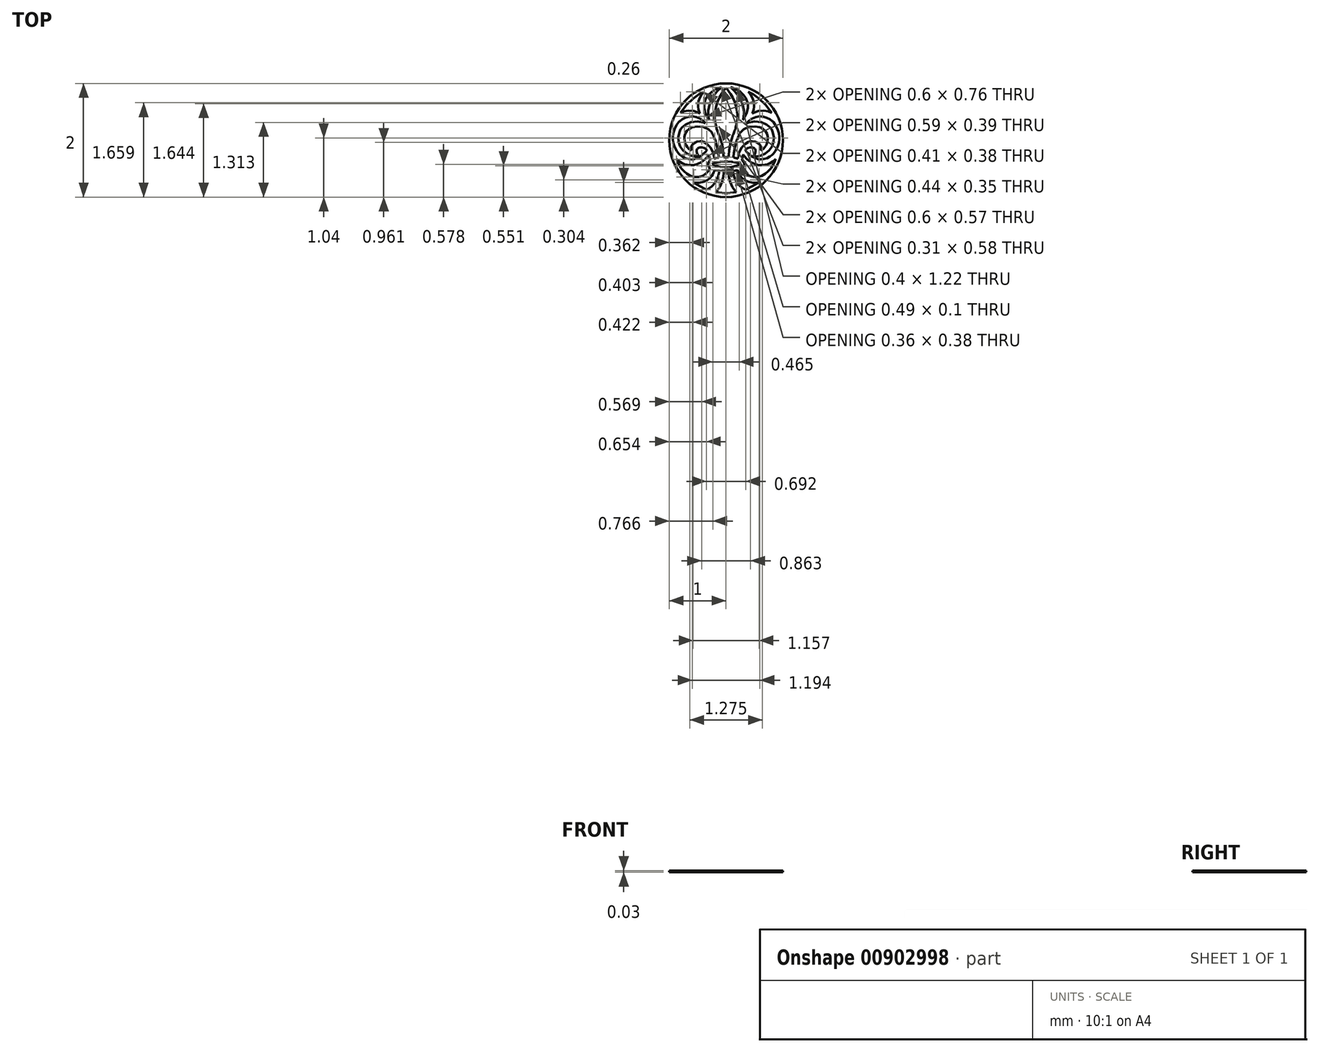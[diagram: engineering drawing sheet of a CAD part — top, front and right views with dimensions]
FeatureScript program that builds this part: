
annotation { "Feature Type Name" : "Feature", "Feature Type Description" : "" }
export const myFeature = defineFeature(function(context is Context, id is Id, definition is map)
    precondition{}
    {
        {
            var Q0;
            Q0=qCreatedBy(makeId("Top.planeOp"),FACE);
            var sketch = newSketch(context, id + "F0", { "sketchPlane" : qUnion([Q0])});
            skLineSegment(sketch, "E0", {"start": v(-0.6, -0.34) * mm, "end": v(-0.58, -0.34) * mm});
            skLineSegment(sketch, "E1", {"start": v(-0.58, -0.34) * mm, "end": v(-0.46, -0.3) * mm});
            skLineSegment(sketch, "E2", {"start": v(-0.46, -0.3) * mm, "end": v(-0.36, -0.2) * mm});
            skLineSegment(sketch, "E3", {"start": v(-0.36, -0.2) * mm, "end": v(-0.34, -0.18) * mm});
            skLineSegment(sketch, "E4", {"start": v(-0.34, -0.18) * mm, "end": v(-0.34, -0.17) * mm});
            skLineSegment(sketch, "E5", {"start": v(-0.34, -0.17) * mm, "end": v(-0.35, -0.16) * mm});
            skLineSegment(sketch, "E6", {"start": v(-0.35, -0.16) * mm, "end": v(-0.37, -0.15) * mm});
            skLineSegment(sketch, "E7", {"start": v(-0.37, -0.15) * mm, "end": v(-0.37, -0.15) * mm});
            skLineSegment(sketch, "E8", {"start": v(-0.37, -0.15) * mm, "end": v(-0.38, -0.14) * mm});
            skLineSegment(sketch, "E9", {"start": v(-0.38, -0.14) * mm, "end": v(-0.42, -0.13) * mm});
            skLineSegment(sketch, "E10", {"start": v(-0.42, -0.13) * mm, "end": v(-0.47, -0.13) * mm});
            skLineSegment(sketch, "E11", {"start": v(-0.47, -0.13) * mm, "end": v(-0.48, -0.13) * mm});
            skLineSegment(sketch, "E12", {"start": v(-0.48, -0.13) * mm, "end": v(-0.48, -0.13) * mm});
            skLineSegment(sketch, "E13", {"start": v(-0.48, -0.13) * mm, "end": v(-0.5, -0.15) * mm});
            skLineSegment(sketch, "E14", {"start": v(-0.5, -0.15) * mm, "end": v(-0.52, -0.17) * mm});
            skLineSegment(sketch, "E15", {"start": v(-0.52, -0.17) * mm, "end": v(-0.52, -0.18) * mm});
            skLineSegment(sketch, "E16", {"start": v(-0.52, -0.18) * mm, "end": v(-0.52, -0.18) * mm});
            skLineSegment(sketch, "E17", {"start": v(-0.52, -0.18) * mm, "end": v(-0.52, -0.2) * mm});
            skLineSegment(sketch, "E18", {"start": v(-0.52, -0.2) * mm, "end": v(-0.51, -0.23) * mm});
            skLineSegment(sketch, "E19", {"start": v(-0.51, -0.23) * mm, "end": v(-0.5, -0.25) * mm});
            skLineSegment(sketch, "E20", {"start": v(-0.5, -0.25) * mm, "end": v(-0.5, -0.26) * mm});
            skLineSegment(sketch, "E21", {"start": v(-0.5, -0.26) * mm, "end": v(-0.5, -0.26) * mm});
            skLineSegment(sketch, "E22", {"start": v(-0.5, -0.26) * mm, "end": v(-0.47, -0.29) * mm});
            skLineSegment(sketch, "E23", {"start": v(-0.47, -0.29) * mm, "end": v(-0.5, -0.29) * mm});
            skLineSegment(sketch, "E24", {"start": v(-0.5, -0.29) * mm, "end": v(-0.53, -0.29) * mm});
            skLineSegment(sketch, "E25", {"start": v(-0.53, -0.29) * mm, "end": v(-0.6, -0.27) * mm});
            skLineSegment(sketch, "E26", {"start": v(-0.6, -0.27) * mm, "end": v(-0.69, -0.23) * mm});
            skLineSegment(sketch, "E27", {"start": v(-0.69, -0.23) * mm, "end": v(-0.76, -0.18) * mm});
            skLineSegment(sketch, "E28", {"start": v(-0.76, -0.18) * mm, "end": v(-0.8, -0.13) * mm});
            skLineSegment(sketch, "E29", {"start": v(-0.8, -0.13) * mm, "end": v(-0.8, -0.1) * mm});
            skLineSegment(sketch, "E30", {"start": v(-0.8, -0.1) * mm, "end": v(-0.82, -0.09) * mm});
            skLineSegment(sketch, "E31", {"start": v(-0.82, -0.09) * mm, "end": v(-0.84, -0.03) * mm});
            skLineSegment(sketch, "E32", {"start": v(-0.84, -0.03) * mm, "end": v(-0.84, 0.05) * mm});
            skLineSegment(sketch, "E33", {"start": v(-0.84, 0.05) * mm, "end": v(-0.83, 0.13) * mm});
            skLineSegment(sketch, "E34", {"start": v(-0.83, 0.13) * mm, "end": v(-0.8, 0.19) * mm});
            skLineSegment(sketch, "E35", {"start": v(-0.8, 0.19) * mm, "end": v(-0.79, 0.2) * mm});
            skLineSegment(sketch, "E36", {"start": v(-0.79, 0.2) * mm, "end": v(-0.77, 0.22) * mm});
            skLineSegment(sketch, "E37", {"start": v(-0.77, 0.22) * mm, "end": v(-0.72, 0.28) * mm});
            skLineSegment(sketch, "E38", {"start": v(-0.72, 0.28) * mm, "end": v(-0.62, 0.32) * mm});
            skLineSegment(sketch, "E39", {"start": v(-0.62, 0.32) * mm, "end": v(-0.5, 0.33) * mm});
            skLineSegment(sketch, "E40", {"start": v(-0.5, 0.33) * mm, "end": v(-0.4, 0.31) * mm});
            skLineSegment(sketch, "E41", {"start": v(-0.4, 0.31) * mm, "end": v(-0.36, 0.3) * mm});
            skLineSegment(sketch, "E42", {"start": v(-0.36, 0.3) * mm, "end": v(-0.37, 0.31) * mm});
            skLineSegment(sketch, "E43", {"start": v(-0.37, 0.31) * mm, "end": v(-0.4, 0.34) * mm});
            skLineSegment(sketch, "E44", {"start": v(-0.4, 0.34) * mm, "end": v(-0.46, 0.38) * mm});
            skLineSegment(sketch, "E45", {"start": v(-0.46, 0.38) * mm, "end": v(-0.52, 0.4) * mm});
            skLineSegment(sketch, "E46", {"start": v(-0.52, 0.4) * mm, "end": v(-0.58, 0.42) * mm});
            skLineSegment(sketch, "E47", {"start": v(-0.58, 0.42) * mm, "end": v(-0.6, 0.42) * mm});
            skLineSegment(sketch, "E48", {"start": v(-0.6, 0.42) * mm, "end": v(-0.62, 0.42) * mm});
            skLineSegment(sketch, "E49", {"start": v(-0.62, 0.42) * mm, "end": v(-0.66, 0.41) * mm});
            skLineSegment(sketch, "E50", {"start": v(-0.66, 0.41) * mm, "end": v(-0.72, 0.4) * mm});
            skLineSegment(sketch, "E51", {"start": v(-0.72, 0.4) * mm, "end": v(-0.77, 0.37) * mm});
            skLineSegment(sketch, "E52", {"start": v(-0.77, 0.37) * mm, "end": v(-0.8, 0.34) * mm});
            skLineSegment(sketch, "E53", {"start": v(-0.8, 0.34) * mm, "end": v(-0.82, 0.33) * mm});
            skLineSegment(sketch, "E54", {"start": v(-0.82, 0.33) * mm, "end": v(-0.83, 0.31) * mm});
            skLineSegment(sketch, "E55", {"start": v(-0.83, 0.31) * mm, "end": v(-0.87, 0.27) * mm});
            skLineSegment(sketch, "E56", {"start": v(-0.87, 0.27) * mm, "end": v(-0.9, 0.2) * mm});
            skLineSegment(sketch, "E57", {"start": v(-0.9, 0.2) * mm, "end": v(-0.93, 0.12) * mm});
            skLineSegment(sketch, "E58", {"start": v(-0.93, 0.12) * mm, "end": v(-0.94, 0.06) * mm});
            skLineSegment(sketch, "E59", {"start": v(-0.94, 0.06) * mm, "end": v(-0.94, 0.04) * mm});
            skLineSegment(sketch, "E60", {"start": v(-0.94, 0.04) * mm, "end": v(-0.94, 0.02) * mm});
            skLineSegment(sketch, "E61", {"start": v(-0.94, 0.02) * mm, "end": v(-0.93, -0.04) * mm});
            skLineSegment(sketch, "E62", {"start": v(-0.93, -0.04) * mm, "end": v(-0.9, -0.12) * mm});
            skLineSegment(sketch, "E63", {"start": v(-0.9, -0.12) * mm, "end": v(-0.87, -0.19) * mm});
            skLineSegment(sketch, "E64", {"start": v(-0.87, -0.19) * mm, "end": v(-0.83, -0.24) * mm});
            skLineSegment(sketch, "E65", {"start": v(-0.83, -0.24) * mm, "end": v(-0.82, -0.25) * mm});
            skLineSegment(sketch, "E66", {"start": v(-0.82, -0.25) * mm, "end": v(-0.8, -0.26) * mm});
            skLineSegment(sketch, "E67", {"start": v(-0.8, -0.26) * mm, "end": v(-0.77, -0.29) * mm});
            skLineSegment(sketch, "E68", {"start": v(-0.77, -0.29) * mm, "end": v(-0.72, -0.32) * mm});
            skLineSegment(sketch, "E69", {"start": v(-0.72, -0.32) * mm, "end": v(-0.66, -0.33) * mm});
            skLineSegment(sketch, "E70", {"start": v(-0.66, -0.33) * mm, "end": v(-0.62, -0.34) * mm});
            skLineSegment(sketch, "E71", {"start": v(-0.62, -0.34) * mm, "end": v(-0.6, -0.34) * mm});
            skLineSegment(sketch, "E72", {"start": v(-0.29, -0.48) * mm, "end": v(-0.3, -0.48) * mm});
            skLineSegment(sketch, "E73", {"start": v(-0.3, -0.48) * mm, "end": v(-0.31, -0.45) * mm});
            skLineSegment(sketch, "E74", {"start": v(-0.31, -0.45) * mm, "end": v(-0.32, -0.43) * mm});
            skLineSegment(sketch, "E75", {"start": v(-0.32, -0.43) * mm, "end": v(-0.32, -0.42) * mm});
            skLineSegment(sketch, "E76", {"start": v(-0.32, -0.42) * mm, "end": v(-0.32, -0.41) * mm});
            skLineSegment(sketch, "E77", {"start": v(-0.32, -0.41) * mm, "end": v(-0.31, -0.4) * mm});
            skLineSegment(sketch, "E78", {"start": v(-0.31, -0.4) * mm, "end": v(-0.3, -0.36) * mm});
            skLineSegment(sketch, "E79", {"start": v(-0.3, -0.36) * mm, "end": v(-0.28, -0.36) * mm});
            skLineSegment(sketch, "E80", {"start": v(-0.28, -0.36) * mm, "end": v(-0.28, -0.35) * mm});
            skLineSegment(sketch, "E81", {"start": v(-0.28, -0.35) * mm, "end": v(-0.29, -0.3) * mm});
            skLineSegment(sketch, "E82", {"start": v(-0.29, -0.3) * mm, "end": v(-0.3, -0.26) * mm});
            skLineSegment(sketch, "E83", {"start": v(-0.3, -0.26) * mm, "end": v(-0.3, -0.25) * mm});
            skLineSegment(sketch, "E84", {"start": v(-0.3, -0.25) * mm, "end": v(-0.31, -0.27) * mm});
            skLineSegment(sketch, "E85", {"start": v(-0.31, -0.27) * mm, "end": v(-0.37, -0.33) * mm});
            skLineSegment(sketch, "E86", {"start": v(-0.37, -0.33) * mm, "end": v(-0.44, -0.39) * mm});
            skLineSegment(sketch, "E87", {"start": v(-0.44, -0.39) * mm, "end": v(-0.5, -0.42) * mm});
            skLineSegment(sketch, "E88", {"start": v(-0.5, -0.42) * mm, "end": v(-0.57, -0.44) * mm});
            skLineSegment(sketch, "E89", {"start": v(-0.57, -0.44) * mm, "end": v(-0.63, -0.44) * mm});
            skLineSegment(sketch, "E90", {"start": v(-0.63, -0.44) * mm, "end": v(-0.68, -0.43) * mm});
            skLineSegment(sketch, "E91", {"start": v(-0.68, -0.43) * mm, "end": v(-0.73, -0.42) * mm});
            skLineSegment(sketch, "E92", {"start": v(-0.73, -0.42) * mm, "end": v(-0.75, -0.42) * mm});
            skLineSegment(sketch, "E93", {"start": v(-0.75, -0.42) * mm, "end": v(-0.76, -0.41) * mm});
            skLineSegment(sketch, "E94", {"start": v(-0.76, -0.41) * mm, "end": v(-0.77, -0.4) * mm});
            skLineSegment(sketch, "E95", {"start": v(-0.77, -0.4) * mm, "end": v(-0.83, -0.37) * mm});
            skLineSegment(sketch, "E96", {"start": v(-0.83, -0.37) * mm, "end": v(-0.87, -0.34) * mm});
            skLineSegment(sketch, "E97", {"start": v(-0.87, -0.34) * mm, "end": v(-0.87, -0.33) * mm});
            skLineSegment(sketch, "E98", {"start": v(-0.87, -0.33) * mm, "end": v(-0.87, -0.34) * mm});
            skLineSegment(sketch, "E99", {"start": v(-0.87, -0.34) * mm, "end": v(-0.85, -0.38) * mm});
            skLineSegment(sketch, "E100", {"start": v(-0.85, -0.38) * mm, "end": v(-0.82, -0.44) * mm});
            skLineSegment(sketch, "E101", {"start": v(-0.82, -0.44) * mm, "end": v(-0.79, -0.5) * mm});
            skLineSegment(sketch, "E102", {"start": v(-0.79, -0.5) * mm, "end": v(-0.74, -0.55) * mm});
            skLineSegment(sketch, "E103", {"start": v(-0.74, -0.55) * mm, "end": v(-0.69, -0.6) * mm});
            skLineSegment(sketch, "E104", {"start": v(-0.69, -0.6) * mm, "end": v(-0.62, -0.63) * mm});
            skLineSegment(sketch, "E105", {"start": v(-0.62, -0.63) * mm, "end": v(-0.55, -0.64) * mm});
            skLineSegment(sketch, "E106", {"start": v(-0.55, -0.64) * mm, "end": v(-0.48, -0.65) * mm});
            skLineSegment(sketch, "E107", {"start": v(-0.48, -0.65) * mm, "end": v(-0.46, -0.64) * mm});
            skLineSegment(sketch, "E108", {"start": v(-0.46, -0.64) * mm, "end": v(-0.44, -0.64) * mm});
            skLineSegment(sketch, "E109", {"start": v(-0.44, -0.64) * mm, "end": v(-0.4, -0.62) * mm});
            skLineSegment(sketch, "E110", {"start": v(-0.4, -0.62) * mm, "end": v(-0.35, -0.59) * mm});
            skLineSegment(sketch, "E111", {"start": v(-0.35, -0.59) * mm, "end": v(-0.31, -0.54) * mm});
            skLineSegment(sketch, "E112", {"start": v(-0.31, -0.54) * mm, "end": v(-0.3, -0.5) * mm});
            skLineSegment(sketch, "E113", {"start": v(-0.3, -0.5) * mm, "end": v(-0.29, -0.48) * mm});
            skLineSegment(sketch, "E114", {"start": v(0.6, -0.34) * mm, "end": v(0.62, -0.34) * mm});
            skLineSegment(sketch, "E115", {"start": v(0.62, -0.34) * mm, "end": v(0.66, -0.33) * mm});
            skLineSegment(sketch, "E116", {"start": v(0.66, -0.33) * mm, "end": v(0.72, -0.32) * mm});
            skLineSegment(sketch, "E117", {"start": v(0.72, -0.32) * mm, "end": v(0.77, -0.29) * mm});
            skLineSegment(sketch, "E118", {"start": v(0.77, -0.29) * mm, "end": v(0.8, -0.26) * mm});
            skLineSegment(sketch, "E119", {"start": v(0.8, -0.26) * mm, "end": v(0.82, -0.25) * mm});
            skLineSegment(sketch, "E120", {"start": v(0.82, -0.25) * mm, "end": v(0.83, -0.24) * mm});
            skLineSegment(sketch, "E121", {"start": v(0.83, -0.24) * mm, "end": v(0.87, -0.19) * mm});
            skLineSegment(sketch, "E122", {"start": v(0.87, -0.19) * mm, "end": v(0.9, -0.12) * mm});
            skLineSegment(sketch, "E123", {"start": v(0.9, -0.12) * mm, "end": v(0.93, -0.04) * mm});
            skLineSegment(sketch, "E124", {"start": v(0.93, -0.04) * mm, "end": v(0.94, 0.02) * mm});
            skLineSegment(sketch, "E125", {"start": v(0.94, 0.02) * mm, "end": v(0.94, 0.04) * mm});
            skLineSegment(sketch, "E126", {"start": v(0.94, 0.04) * mm, "end": v(0.94, 0.06) * mm});
            skLineSegment(sketch, "E127", {"start": v(0.94, 0.06) * mm, "end": v(0.93, 0.12) * mm});
            skLineSegment(sketch, "E128", {"start": v(0.93, 0.12) * mm, "end": v(0.9, 0.2) * mm});
            skLineSegment(sketch, "E129", {"start": v(0.9, 0.2) * mm, "end": v(0.87, 0.27) * mm});
            skLineSegment(sketch, "E130", {"start": v(0.87, 0.27) * mm, "end": v(0.83, 0.31) * mm});
            skLineSegment(sketch, "E131", {"start": v(0.83, 0.31) * mm, "end": v(0.82, 0.33) * mm});
            skLineSegment(sketch, "E132", {"start": v(0.82, 0.33) * mm, "end": v(0.8, 0.34) * mm});
            skLineSegment(sketch, "E133", {"start": v(0.8, 0.34) * mm, "end": v(0.77, 0.37) * mm});
            skLineSegment(sketch, "E134", {"start": v(0.77, 0.37) * mm, "end": v(0.72, 0.4) * mm});
            skLineSegment(sketch, "E135", {"start": v(0.72, 0.4) * mm, "end": v(0.66, 0.41) * mm});
            skLineSegment(sketch, "E136", {"start": v(0.66, 0.41) * mm, "end": v(0.62, 0.42) * mm});
            skLineSegment(sketch, "E137", {"start": v(0.62, 0.42) * mm, "end": v(0.6, 0.42) * mm});
            skLineSegment(sketch, "E138", {"start": v(0.6, 0.42) * mm, "end": v(0.58, 0.42) * mm});
            skLineSegment(sketch, "E139", {"start": v(0.58, 0.42) * mm, "end": v(0.52, 0.4) * mm});
            skLineSegment(sketch, "E140", {"start": v(0.52, 0.4) * mm, "end": v(0.46, 0.38) * mm});
            skLineSegment(sketch, "E141", {"start": v(0.46, 0.38) * mm, "end": v(0.4, 0.34) * mm});
            skLineSegment(sketch, "E142", {"start": v(0.4, 0.34) * mm, "end": v(0.37, 0.31) * mm});
            skLineSegment(sketch, "E143", {"start": v(0.37, 0.31) * mm, "end": v(0.36, 0.3) * mm});
            skLineSegment(sketch, "E144", {"start": v(0.36, 0.3) * mm, "end": v(0.4, 0.31) * mm});
            skLineSegment(sketch, "E145", {"start": v(0.4, 0.31) * mm, "end": v(0.5, 0.33) * mm});
            skLineSegment(sketch, "E146", {"start": v(0.5, 0.33) * mm, "end": v(0.62, 0.32) * mm});
            skLineSegment(sketch, "E147", {"start": v(0.62, 0.32) * mm, "end": v(0.72, 0.28) * mm});
            skLineSegment(sketch, "E148", {"start": v(0.72, 0.28) * mm, "end": v(0.77, 0.22) * mm});
            skLineSegment(sketch, "E149", {"start": v(0.77, 0.22) * mm, "end": v(0.79, 0.2) * mm});
            skLineSegment(sketch, "E150", {"start": v(0.79, 0.2) * mm, "end": v(0.8, 0.19) * mm});
            skLineSegment(sketch, "E151", {"start": v(0.8, 0.19) * mm, "end": v(0.83, 0.13) * mm});
            skLineSegment(sketch, "E152", {"start": v(0.83, 0.13) * mm, "end": v(0.84, 0.05) * mm});
            skLineSegment(sketch, "E153", {"start": v(0.84, 0.05) * mm, "end": v(0.84, -0.03) * mm});
            skLineSegment(sketch, "E154", {"start": v(0.84, -0.03) * mm, "end": v(0.82, -0.09) * mm});
            skLineSegment(sketch, "E155", {"start": v(0.82, -0.09) * mm, "end": v(0.8, -0.1) * mm});
            skLineSegment(sketch, "E156", {"start": v(0.8, -0.1) * mm, "end": v(0.8, -0.13) * mm});
            skLineSegment(sketch, "E157", {"start": v(0.8, -0.13) * mm, "end": v(0.76, -0.18) * mm});
            skLineSegment(sketch, "E158", {"start": v(0.76, -0.18) * mm, "end": v(0.69, -0.23) * mm});
            skLineSegment(sketch, "E159", {"start": v(0.69, -0.23) * mm, "end": v(0.6, -0.27) * mm});
            skLineSegment(sketch, "E160", {"start": v(0.6, -0.27) * mm, "end": v(0.53, -0.29) * mm});
            skLineSegment(sketch, "E161", {"start": v(0.53, -0.29) * mm, "end": v(0.5, -0.29) * mm});
            skLineSegment(sketch, "E162", {"start": v(0.5, -0.29) * mm, "end": v(0.47, -0.29) * mm});
            skLineSegment(sketch, "E163", {"start": v(0.47, -0.29) * mm, "end": v(0.5, -0.26) * mm});
            skLineSegment(sketch, "E164", {"start": v(0.5, -0.26) * mm, "end": v(0.5, -0.26) * mm});
            skLineSegment(sketch, "E165", {"start": v(0.5, -0.26) * mm, "end": v(0.5, -0.25) * mm});
            skLineSegment(sketch, "E166", {"start": v(0.5, -0.25) * mm, "end": v(0.51, -0.23) * mm});
            skLineSegment(sketch, "E167", {"start": v(0.51, -0.23) * mm, "end": v(0.52, -0.2) * mm});
            skLineSegment(sketch, "E168", {"start": v(0.52, -0.2) * mm, "end": v(0.52, -0.18) * mm});
            skLineSegment(sketch, "E169", {"start": v(0.52, -0.18) * mm, "end": v(0.52, -0.18) * mm});
            skLineSegment(sketch, "E170", {"start": v(0.52, -0.18) * mm, "end": v(0.52, -0.17) * mm});
            skLineSegment(sketch, "E171", {"start": v(0.52, -0.17) * mm, "end": v(0.5, -0.15) * mm});
            skLineSegment(sketch, "E172", {"start": v(0.5, -0.15) * mm, "end": v(0.48, -0.13) * mm});
            skLineSegment(sketch, "E173", {"start": v(0.48, -0.13) * mm, "end": v(0.48, -0.13) * mm});
            skLineSegment(sketch, "E174", {"start": v(0.48, -0.13) * mm, "end": v(0.47, -0.13) * mm});
            skLineSegment(sketch, "E175", {"start": v(0.47, -0.13) * mm, "end": v(0.42, -0.13) * mm});
            skLineSegment(sketch, "E176", {"start": v(0.42, -0.13) * mm, "end": v(0.38, -0.14) * mm});
            skLineSegment(sketch, "E177", {"start": v(0.38, -0.14) * mm, "end": v(0.37, -0.15) * mm});
            skLineSegment(sketch, "E178", {"start": v(0.37, -0.15) * mm, "end": v(0.37, -0.15) * mm});
            skLineSegment(sketch, "E179", {"start": v(0.37, -0.15) * mm, "end": v(0.35, -0.16) * mm});
            skLineSegment(sketch, "E180", {"start": v(0.35, -0.16) * mm, "end": v(0.34, -0.17) * mm});
            skLineSegment(sketch, "E181", {"start": v(0.34, -0.17) * mm, "end": v(0.34, -0.18) * mm});
            skLineSegment(sketch, "E182", {"start": v(0.34, -0.18) * mm, "end": v(0.36, -0.2) * mm});
            skLineSegment(sketch, "E183", {"start": v(0.36, -0.2) * mm, "end": v(0.46, -0.3) * mm});
            skLineSegment(sketch, "E184", {"start": v(0.46, -0.3) * mm, "end": v(0.58, -0.34) * mm});
            skLineSegment(sketch, "E185", {"start": v(0.58, -0.34) * mm, "end": v(0.6, -0.34) * mm});
            skLineSegment(sketch, "E186", {"start": v(-0.17, 0.2) * mm, "end": v(-0.12, 0.1) * mm});
            skLineSegment(sketch, "E187", {"start": v(-0.12, 0.1) * mm, "end": v(-0.12, 0.08) * mm});
            skLineSegment(sketch, "E188", {"start": v(-0.12, 0.08) * mm, "end": v(-0.1, 0.02) * mm});
            skLineSegment(sketch, "E189", {"start": v(-0.1, 0.02) * mm, "end": v(-0.08, -0.04) * mm});
            skLineSegment(sketch, "E190", {"start": v(-0.08, -0.04) * mm, "end": v(-0.08, -0.06) * mm});
            skLineSegment(sketch, "E191", {"start": v(-0.08, -0.06) * mm, "end": v(-0.07, -0.08) * mm});
            skLineSegment(sketch, "E192", {"start": v(-0.07, -0.08) * mm, "end": v(-0.05, -0.18) * mm});
            skLineSegment(sketch, "E193", {"start": v(-0.05, -0.18) * mm, "end": v(-0.04, -0.27) * mm});
            skLineSegment(sketch, "E194", {"start": v(-0.04, -0.27) * mm, "end": v(-0.04, -0.28) * mm});
            skLineSegment(sketch, "E195", {"start": v(-0.04, -0.28) * mm, "end": v(-0.04, -0.3) * mm});
            skLineSegment(sketch, "E196", {"start": v(-0.04, -0.3) * mm, "end": v(-0.04, -0.3) * mm});
            skLineSegment(sketch, "E197", {"start": v(-0.04, -0.3) * mm, "end": v(-0.02, -0.3) * mm});
            skLineSegment(sketch, "E198", {"start": v(-0.02, -0.3) * mm, "end": v(0, -0.3) * mm});
            skLineSegment(sketch, "E199", {"start": v(0, -0.3) * mm, "end": v(0, -0.3) * mm});
            skLineSegment(sketch, "E200", {"start": v(0, -0.3) * mm, "end": v(0.02, -0.3) * mm});
            skLineSegment(sketch, "E201", {"start": v(0.02, -0.3) * mm, "end": v(0.04, -0.3) * mm});
            skLineSegment(sketch, "E202", {"start": v(0.04, -0.3) * mm, "end": v(0.04, -0.3) * mm});
            skLineSegment(sketch, "E203", {"start": v(0.04, -0.3) * mm, "end": v(0.04, -0.28) * mm});
            skLineSegment(sketch, "E204", {"start": v(0.04, -0.28) * mm, "end": v(0.04, -0.27) * mm});
            skLineSegment(sketch, "E205", {"start": v(0.04, -0.27) * mm, "end": v(0.05, -0.18) * mm});
            skLineSegment(sketch, "E206", {"start": v(0.05, -0.18) * mm, "end": v(0.07, -0.08) * mm});
            skLineSegment(sketch, "E207", {"start": v(0.07, -0.08) * mm, "end": v(0.08, -0.06) * mm});
            skLineSegment(sketch, "E208", {"start": v(0.08, -0.06) * mm, "end": v(0.08, -0.04) * mm});
            skLineSegment(sketch, "E209", {"start": v(0.08, -0.04) * mm, "end": v(0.1, 0.02) * mm});
            skLineSegment(sketch, "E210", {"start": v(0.1, 0.02) * mm, "end": v(0.12, 0.08) * mm});
            skLineSegment(sketch, "E211", {"start": v(0.12, 0.08) * mm, "end": v(0.12, 0.1) * mm});
            skLineSegment(sketch, "E212", {"start": v(0.12, 0.1) * mm, "end": v(0.13, 0.1) * mm});
            skLineSegment(sketch, "E213", {"start": v(0.13, 0.1) * mm, "end": v(0.13, 0.1) * mm});
            skLineSegment(sketch, "E214", {"start": v(0.13, 0.1) * mm, "end": v(0.14, 0.13) * mm});
            skLineSegment(sketch, "E215", {"start": v(0.14, 0.13) * mm, "end": v(0.14, 0.15) * mm});
            skLineSegment(sketch, "E216", {"start": v(0.14, 0.15) * mm, "end": v(0.15, 0.17) * mm});
            skLineSegment(sketch, "E217", {"start": v(0.15, 0.17) * mm, "end": v(0.16, 0.19) * mm});
            skLineSegment(sketch, "E218", {"start": v(0.16, 0.19) * mm, "end": v(0.16, 0.2) * mm});
            skLineSegment(sketch, "E219", {"start": v(0.16, 0.2) * mm, "end": v(0.17, 0.2) * mm});
            skLineSegment(sketch, "E220", {"start": v(0.17, 0.2) * mm, "end": v(0.17, 0.2) * mm});
            skLineSegment(sketch, "E221", {"start": v(0.17, 0.2) * mm, "end": v(0.17, 0.22) * mm});
            skLineSegment(sketch, "E222", {"start": v(0.17, 0.22) * mm, "end": v(0.2, 0.31) * mm});
            skLineSegment(sketch, "E223", {"start": v(0.2, 0.31) * mm, "end": v(0.2, 0.39) * mm});
            skLineSegment(sketch, "E224", {"start": v(0.2, 0.39) * mm, "end": v(0.2, 0.41) * mm});
            skLineSegment(sketch, "E225", {"start": v(0.2, 0.41) * mm, "end": v(0.2, 0.44) * mm});
            skLineSegment(sketch, "E226", {"start": v(0.2, 0.44) * mm, "end": v(0.2, 0.5) * mm});
            skLineSegment(sketch, "E227", {"start": v(0.2, 0.5) * mm, "end": v(0.17, 0.6) * mm});
            skLineSegment(sketch, "E228", {"start": v(0.17, 0.6) * mm, "end": v(0.15, 0.68) * mm});
            skLineSegment(sketch, "E229", {"start": v(0.15, 0.68) * mm, "end": v(0.11, 0.75) * mm});
            skLineSegment(sketch, "E230", {"start": v(0.11, 0.75) * mm, "end": v(0.08, 0.81) * mm});
            skLineSegment(sketch, "E231", {"start": v(0.08, 0.81) * mm, "end": v(0.05, 0.86) * mm});
            skLineSegment(sketch, "E232", {"start": v(0.05, 0.86) * mm, "end": v(0.02, 0.9) * mm});
            skLineSegment(sketch, "E233", {"start": v(0.02, 0.9) * mm, "end": v(0, 0.92) * mm});
            skLineSegment(sketch, "E234", {"start": v(0, 0.92) * mm, "end": v(0, 0.92) * mm});
            skLineSegment(sketch, "E235", {"start": v(0, 0.92) * mm, "end": v(-0.02, 0.9) * mm});
            skLineSegment(sketch, "E236", {"start": v(-0.02, 0.9) * mm, "end": v(-0.05, 0.86) * mm});
            skLineSegment(sketch, "E237", {"start": v(-0.05, 0.86) * mm, "end": v(-0.08, 0.81) * mm});
            skLineSegment(sketch, "E238", {"start": v(-0.08, 0.81) * mm, "end": v(-0.11, 0.75) * mm});
            skLineSegment(sketch, "E239", {"start": v(-0.11, 0.75) * mm, "end": v(-0.15, 0.68) * mm});
            skLineSegment(sketch, "E240", {"start": v(-0.15, 0.68) * mm, "end": v(-0.17, 0.6) * mm});
            skLineSegment(sketch, "E241", {"start": v(-0.17, 0.6) * mm, "end": v(-0.2, 0.5) * mm});
            skLineSegment(sketch, "E242", {"start": v(-0.2, 0.5) * mm, "end": v(-0.2, 0.44) * mm});
            skLineSegment(sketch, "E243", {"start": v(-0.2, 0.44) * mm, "end": v(-0.2, 0.41) * mm});
            skLineSegment(sketch, "E244", {"start": v(-0.2, 0.41) * mm, "end": v(-0.2, 0.39) * mm});
            skLineSegment(sketch, "E245", {"start": v(-0.2, 0.39) * mm, "end": v(-0.2, 0.31) * mm});
            skLineSegment(sketch, "E246", {"start": v(-0.2, 0.31) * mm, "end": v(-0.17, 0.22) * mm});
            skLineSegment(sketch, "E247", {"start": v(-0.17, 0.22) * mm, "end": v(-0.17, 0.2) * mm});
            skLineSegment(sketch, "E248", {"start": v(-0.46, 0.47) * mm, "end": v(-0.46, 0.48) * mm});
            skLineSegment(sketch, "E249", {"start": v(-0.46, 0.48) * mm, "end": v(-0.49, 0.54) * mm});
            skLineSegment(sketch, "E250", {"start": v(-0.49, 0.54) * mm, "end": v(-0.5, 0.6) * mm});
            skLineSegment(sketch, "E251", {"start": v(-0.5, 0.6) * mm, "end": v(-0.5, 0.61) * mm});
            skLineSegment(sketch, "E252", {"start": v(-0.5, 0.61) * mm, "end": v(-0.5, 0.63) * mm});
            skLineSegment(sketch, "E253", {"start": v(-0.5, 0.63) * mm, "end": v(-0.48, 0.69) * mm});
            skLineSegment(sketch, "E254", {"start": v(-0.48, 0.69) * mm, "end": v(-0.46, 0.75) * mm});
            skLineSegment(sketch, "E255", {"start": v(-0.46, 0.75) * mm, "end": v(-0.43, 0.8) * mm});
            skLineSegment(sketch, "E256", {"start": v(-0.43, 0.8) * mm, "end": v(-0.4, 0.84) * mm});
            skLineSegment(sketch, "E257", {"start": v(-0.4, 0.84) * mm, "end": v(-0.4, 0.85) * mm});
            skLineSegment(sketch, "E258", {"start": v(-0.4, 0.85) * mm, "end": v(-0.42, 0.84) * mm});
            skLineSegment(sketch, "E259", {"start": v(-0.42, 0.84) * mm, "end": v(-0.48, 0.8) * mm});
            skLineSegment(sketch, "E260", {"start": v(-0.48, 0.8) * mm, "end": v(-0.58, 0.73) * mm});
            skLineSegment(sketch, "E261", {"start": v(-0.58, 0.73) * mm, "end": v(-0.7, 0.62) * mm});
            skLineSegment(sketch, "E262", {"start": v(-0.7, 0.62) * mm, "end": v(-0.78, 0.52) * mm});
            skLineSegment(sketch, "E263", {"start": v(-0.78, 0.52) * mm, "end": v(-0.8, 0.48) * mm});
            skLineSegment(sketch, "E264", {"start": v(-0.8, 0.48) * mm, "end": v(-0.79, 0.49) * mm});
            skLineSegment(sketch, "E265", {"start": v(-0.79, 0.49) * mm, "end": v(-0.74, 0.5) * mm});
            skLineSegment(sketch, "E266", {"start": v(-0.74, 0.5) * mm, "end": v(-0.67, 0.52) * mm});
            skLineSegment(sketch, "E267", {"start": v(-0.67, 0.52) * mm, "end": v(-0.57, 0.51) * mm});
            skLineSegment(sketch, "E268", {"start": v(-0.57, 0.51) * mm, "end": v(-0.48, 0.48) * mm});
            skLineSegment(sketch, "E269", {"start": v(-0.48, 0.48) * mm, "end": v(-0.46, 0.47) * mm});
            skLineSegment(sketch, "E270", {"start": v(0, -0.47) * mm, "end": v(0.03, -0.47) * mm});
            skLineSegment(sketch, "E271", {"start": v(0.03, -0.47) * mm, "end": v(0.1, -0.47) * mm});
            skLineSegment(sketch, "E272", {"start": v(0.1, -0.47) * mm, "end": v(0.18, -0.45) * mm});
            skLineSegment(sketch, "E273", {"start": v(0.18, -0.45) * mm, "end": v(0.22, -0.44) * mm});
            skLineSegment(sketch, "E274", {"start": v(0.22, -0.44) * mm, "end": v(0.24, -0.43) * mm});
            skLineSegment(sketch, "E275", {"start": v(0.24, -0.43) * mm, "end": v(0.24, -0.42) * mm});
            skLineSegment(sketch, "E276", {"start": v(0.24, -0.42) * mm, "end": v(0.24, -0.42) * mm});
            skLineSegment(sketch, "E277", {"start": v(0.24, -0.42) * mm, "end": v(0.22, -0.4) * mm});
            skLineSegment(sketch, "E278", {"start": v(0.22, -0.4) * mm, "end": v(0.18, -0.4) * mm});
            skLineSegment(sketch, "E279", {"start": v(0.18, -0.4) * mm, "end": v(0.1, -0.38) * mm});
            skLineSegment(sketch, "E280", {"start": v(0.1, -0.38) * mm, "end": v(0.03, -0.37) * mm});
            skLineSegment(sketch, "E281", {"start": v(0.03, -0.37) * mm, "end": v(0, -0.37) * mm});
            skLineSegment(sketch, "E282", {"start": v(0, -0.37) * mm, "end": v(0, -0.37) * mm});
            skLineSegment(sketch, "E283", {"start": v(0, -0.37) * mm, "end": v(-0.03, -0.37) * mm});
            skLineSegment(sketch, "E284", {"start": v(-0.03, -0.37) * mm, "end": v(-0.1, -0.38) * mm});
            skLineSegment(sketch, "E285", {"start": v(-0.1, -0.38) * mm, "end": v(-0.18, -0.4) * mm});
            skLineSegment(sketch, "E286", {"start": v(-0.18, -0.4) * mm, "end": v(-0.22, -0.4) * mm});
            skLineSegment(sketch, "E287", {"start": v(-0.22, -0.4) * mm, "end": v(-0.24, -0.42) * mm});
            skLineSegment(sketch, "E288", {"start": v(-0.24, -0.42) * mm, "end": v(-0.24, -0.42) * mm});
            skLineSegment(sketch, "E289", {"start": v(-0.24, -0.42) * mm, "end": v(-0.24, -0.43) * mm});
            skLineSegment(sketch, "E290", {"start": v(-0.24, -0.43) * mm, "end": v(-0.22, -0.44) * mm});
            skLineSegment(sketch, "E291", {"start": v(-0.22, -0.44) * mm, "end": v(-0.18, -0.45) * mm});
            skLineSegment(sketch, "E292", {"start": v(-0.18, -0.45) * mm, "end": v(-0.1, -0.47) * mm});
            skLineSegment(sketch, "E293", {"start": v(-0.1, -0.47) * mm, "end": v(-0.03, -0.47) * mm});
            skLineSegment(sketch, "E294", {"start": v(-0.03, -0.47) * mm, "end": v(0, -0.47) * mm});
            skLineSegment(sketch, "E295", {"start": v(0, -0.47) * mm, "end": v(0, -0.47) * mm});
            skLineSegment(sketch, "E296", {"start": v(-0.21, -0.55) * mm, "end": v(-0.21, -0.55) * mm});
            skLineSegment(sketch, "E297", {"start": v(-0.21, -0.55) * mm, "end": v(-0.22, -0.57) * mm});
            skLineSegment(sketch, "E298", {"start": v(-0.22, -0.57) * mm, "end": v(-0.23, -0.6) * mm});
            skLineSegment(sketch, "E299", {"start": v(-0.23, -0.6) * mm, "end": v(-0.25, -0.63) * mm});
            skLineSegment(sketch, "E300", {"start": v(-0.25, -0.63) * mm, "end": v(-0.28, -0.67) * mm});
            skLineSegment(sketch, "E301", {"start": v(-0.28, -0.67) * mm, "end": v(-0.33, -0.7) * mm});
            skLineSegment(sketch, "E302", {"start": v(-0.33, -0.7) * mm, "end": v(-0.4, -0.73) * mm});
            skLineSegment(sketch, "E303", {"start": v(-0.4, -0.73) * mm, "end": v(-0.47, -0.75) * mm});
            skLineSegment(sketch, "E304", {"start": v(-0.47, -0.75) * mm, "end": v(-0.54, -0.75) * mm});
            skLineSegment(sketch, "E305", {"start": v(-0.54, -0.75) * mm, "end": v(-0.57, -0.74) * mm});
            skLineSegment(sketch, "E306", {"start": v(-0.57, -0.74) * mm, "end": v(-0.56, -0.75) * mm});
            skLineSegment(sketch, "E307", {"start": v(-0.56, -0.75) * mm, "end": v(-0.47, -0.8) * mm});
            skLineSegment(sketch, "E308", {"start": v(-0.47, -0.8) * mm, "end": v(-0.36, -0.86) * mm});
            skLineSegment(sketch, "E309", {"start": v(-0.36, -0.86) * mm, "end": v(-0.34, -0.87) * mm});
            skLineSegment(sketch, "E310", {"start": v(-0.34, -0.87) * mm, "end": v(-0.31, -0.86) * mm});
            skLineSegment(sketch, "E311", {"start": v(-0.31, -0.86) * mm, "end": v(-0.25, -0.81) * mm});
            skLineSegment(sketch, "E312", {"start": v(-0.25, -0.81) * mm, "end": v(-0.19, -0.74) * mm});
            skLineSegment(sketch, "E313", {"start": v(-0.19, -0.74) * mm, "end": v(-0.14, -0.65) * mm});
            skLineSegment(sketch, "E314", {"start": v(-0.14, -0.65) * mm, "end": v(-0.13, -0.57) * mm});
            skLineSegment(sketch, "E315", {"start": v(-0.13, -0.57) * mm, "end": v(-0.12, -0.54) * mm});
            skLineSegment(sketch, "E316", {"start": v(-0.12, -0.54) * mm, "end": v(-0.13, -0.54) * mm});
            skLineSegment(sketch, "E317", {"start": v(-0.13, -0.54) * mm, "end": v(-0.2, -0.53) * mm});
            skLineSegment(sketch, "E318", {"start": v(-0.2, -0.53) * mm, "end": v(-0.2, -0.52) * mm});
            skLineSegment(sketch, "E319", {"start": v(-0.2, -0.52) * mm, "end": v(-0.2, -0.53) * mm});
            skLineSegment(sketch, "E320", {"start": v(-0.2, -0.53) * mm, "end": v(-0.2, -0.54) * mm});
            skLineSegment(sketch, "E321", {"start": v(-0.2, -0.54) * mm, "end": v(-0.21, -0.55) * mm});
            skLineSegment(sketch, "E322", {"start": v(-0.41, -0.03) * mm, "end": v(-0.4, -0.03) * mm});
            skLineSegment(sketch, "E323", {"start": v(-0.4, -0.03) * mm, "end": v(-0.34, -0.06) * mm});
            skLineSegment(sketch, "E324", {"start": v(-0.34, -0.06) * mm, "end": v(-0.28, -0.12) * mm});
            skLineSegment(sketch, "E325", {"start": v(-0.28, -0.12) * mm, "end": v(-0.23, -0.2) * mm});
            skLineSegment(sketch, "E326", {"start": v(-0.23, -0.2) * mm, "end": v(-0.21, -0.29) * mm});
            skLineSegment(sketch, "E327", {"start": v(-0.21, -0.29) * mm, "end": v(-0.2, -0.31) * mm});
            skLineSegment(sketch, "E328", {"start": v(-0.2, -0.31) * mm, "end": v(-0.2, -0.32) * mm});
            skLineSegment(sketch, "E329", {"start": v(-0.2, -0.32) * mm, "end": v(-0.2, -0.32) * mm});
            skLineSegment(sketch, "E330", {"start": v(-0.2, -0.32) * mm, "end": v(-0.14, -0.3) * mm});
            skLineSegment(sketch, "E331", {"start": v(-0.14, -0.3) * mm, "end": v(-0.13, -0.3) * mm});
            skLineSegment(sketch, "E332", {"start": v(-0.13, -0.3) * mm, "end": v(-0.13, -0.29) * mm});
            skLineSegment(sketch, "E333", {"start": v(-0.13, -0.29) * mm, "end": v(-0.14, -0.23) * mm});
            skLineSegment(sketch, "E334", {"start": v(-0.14, -0.23) * mm, "end": v(-0.15, -0.13) * mm});
            skLineSegment(sketch, "E335", {"start": v(-0.15, -0.13) * mm, "end": v(-0.19, 0) * mm});
            skLineSegment(sketch, "E336", {"start": v(-0.19, 0) * mm, "end": v(-0.23, 0.09) * mm});
            skLineSegment(sketch, "E337", {"start": v(-0.23, 0.09) * mm, "end": v(-0.24, 0.11) * mm});
            skLineSegment(sketch, "E338", {"start": v(-0.24, 0.11) * mm, "end": v(-0.25, 0.14) * mm});
            skLineSegment(sketch, "E339", {"start": v(-0.25, 0.14) * mm, "end": v(-0.3, 0.2) * mm});
            skLineSegment(sketch, "E340", {"start": v(-0.3, 0.2) * mm, "end": v(-0.4, 0.24) * mm});
            skLineSegment(sketch, "E341", {"start": v(-0.4, 0.24) * mm, "end": v(-0.51, 0.24) * mm});
            skLineSegment(sketch, "E342", {"start": v(-0.51, 0.24) * mm, "end": v(-0.59, 0.23) * mm});
            skLineSegment(sketch, "E343", {"start": v(-0.59, 0.23) * mm, "end": v(-0.61, 0.22) * mm});
            skLineSegment(sketch, "E344", {"start": v(-0.61, 0.22) * mm, "end": v(-0.62, 0.22) * mm});
            skLineSegment(sketch, "E345", {"start": v(-0.62, 0.22) * mm, "end": v(-0.65, 0.2) * mm});
            skLineSegment(sketch, "E346", {"start": v(-0.65, 0.2) * mm, "end": v(-0.69, 0.16) * mm});
            skLineSegment(sketch, "E347", {"start": v(-0.69, 0.16) * mm, "end": v(-0.72, 0.11) * mm});
            skLineSegment(sketch, "E348", {"start": v(-0.72, 0.11) * mm, "end": v(-0.73, 0.06) * mm});
            skLineSegment(sketch, "E349", {"start": v(-0.73, 0.06) * mm, "end": v(-0.73, 0.04) * mm});
            skLineSegment(sketch, "E350", {"start": v(-0.73, 0.04) * mm, "end": v(-0.73, 0.02) * mm});
            skLineSegment(sketch, "E351", {"start": v(-0.73, 0.02) * mm, "end": v(-0.73, -0.02) * mm});
            skLineSegment(sketch, "E352", {"start": v(-0.73, -0.02) * mm, "end": v(-0.71, -0.07) * mm});
            skLineSegment(sketch, "E353", {"start": v(-0.71, -0.07) * mm, "end": v(-0.7, -0.08) * mm});
            skLineSegment(sketch, "E354", {"start": v(-0.7, -0.08) * mm, "end": v(-0.7, -0.1) * mm});
            skLineSegment(sketch, "E355", {"start": v(-0.7, -0.1) * mm, "end": v(-0.68, -0.12) * mm});
            skLineSegment(sketch, "E356", {"start": v(-0.68, -0.12) * mm, "end": v(-0.66, -0.15) * mm});
            skLineSegment(sketch, "E357", {"start": v(-0.66, -0.15) * mm, "end": v(-0.63, -0.17) * mm});
            skLineSegment(sketch, "E358", {"start": v(-0.63, -0.17) * mm, "end": v(-0.61, -0.18) * mm});
            skLineSegment(sketch, "E359", {"start": v(-0.61, -0.18) * mm, "end": v(-0.6, -0.18) * mm});
            skLineSegment(sketch, "E360", {"start": v(-0.6, -0.18) * mm, "end": v(-0.6, -0.18) * mm});
            skLineSegment(sketch, "E361", {"start": v(-0.6, -0.18) * mm, "end": v(-0.61, -0.15) * mm});
            skLineSegment(sketch, "E362", {"start": v(-0.61, -0.15) * mm, "end": v(-0.61, -0.15) * mm});
            skLineSegment(sketch, "E363", {"start": v(-0.61, -0.15) * mm, "end": v(-0.61, -0.14) * mm});
            skLineSegment(sketch, "E364", {"start": v(-0.61, -0.14) * mm, "end": v(-0.6, -0.1) * mm});
            skLineSegment(sketch, "E365", {"start": v(-0.6, -0.1) * mm, "end": v(-0.6, -0.08) * mm});
            skLineSegment(sketch, "E366", {"start": v(-0.6, -0.08) * mm, "end": v(-0.59, -0.07) * mm});
            skLineSegment(sketch, "E367", {"start": v(-0.59, -0.07) * mm, "end": v(-0.58, -0.06) * mm});
            skLineSegment(sketch, "E368", {"start": v(-0.58, -0.06) * mm, "end": v(-0.55, -0.04) * mm});
            skLineSegment(sketch, "E369", {"start": v(-0.55, -0.04) * mm, "end": v(-0.5, -0.02) * mm});
            skLineSegment(sketch, "E370", {"start": v(-0.5, -0.02) * mm, "end": v(-0.46, -0.02) * mm});
            skLineSegment(sketch, "E371", {"start": v(-0.46, -0.02) * mm, "end": v(-0.42, -0.02) * mm});
            skLineSegment(sketch, "E372", {"start": v(-0.42, -0.02) * mm, "end": v(-0.41, -0.03) * mm});
            skLineSegment(sketch, "E373", {"start": v(0.59, -0.07) * mm, "end": v(0.6, -0.08) * mm});
            skLineSegment(sketch, "E374", {"start": v(0.6, -0.08) * mm, "end": v(0.6, -0.1) * mm});
            skLineSegment(sketch, "E375", {"start": v(0.6, -0.1) * mm, "end": v(0.61, -0.14) * mm});
            skLineSegment(sketch, "E376", {"start": v(0.61, -0.14) * mm, "end": v(0.61, -0.15) * mm});
            skLineSegment(sketch, "E377", {"start": v(0.61, -0.15) * mm, "end": v(0.61, -0.15) * mm});
            skLineSegment(sketch, "E378", {"start": v(0.61, -0.15) * mm, "end": v(0.6, -0.18) * mm});
            skLineSegment(sketch, "E379", {"start": v(0.6, -0.18) * mm, "end": v(0.6, -0.18) * mm});
            skLineSegment(sketch, "E380", {"start": v(0.6, -0.18) * mm, "end": v(0.61, -0.18) * mm});
            skLineSegment(sketch, "E381", {"start": v(0.61, -0.18) * mm, "end": v(0.63, -0.17) * mm});
            skLineSegment(sketch, "E382", {"start": v(0.63, -0.17) * mm, "end": v(0.66, -0.15) * mm});
            skLineSegment(sketch, "E383", {"start": v(0.66, -0.15) * mm, "end": v(0.68, -0.12) * mm});
            skLineSegment(sketch, "E384", {"start": v(0.68, -0.12) * mm, "end": v(0.7, -0.1) * mm});
            skLineSegment(sketch, "E385", {"start": v(0.7, -0.1) * mm, "end": v(0.7, -0.08) * mm});
            skLineSegment(sketch, "E386", {"start": v(0.7, -0.08) * mm, "end": v(0.71, -0.07) * mm});
            skLineSegment(sketch, "E387", {"start": v(0.71, -0.07) * mm, "end": v(0.73, -0.02) * mm});
            skLineSegment(sketch, "E388", {"start": v(0.73, -0.02) * mm, "end": v(0.73, 0.02) * mm});
            skLineSegment(sketch, "E389", {"start": v(0.73, 0.02) * mm, "end": v(0.73, 0.04) * mm});
            skLineSegment(sketch, "E390", {"start": v(0.73, 0.04) * mm, "end": v(0.73, 0.06) * mm});
            skLineSegment(sketch, "E391", {"start": v(0.73, 0.06) * mm, "end": v(0.72, 0.11) * mm});
            skLineSegment(sketch, "E392", {"start": v(0.72, 0.11) * mm, "end": v(0.69, 0.16) * mm});
            skLineSegment(sketch, "E393", {"start": v(0.69, 0.16) * mm, "end": v(0.65, 0.2) * mm});
            skLineSegment(sketch, "E394", {"start": v(0.65, 0.2) * mm, "end": v(0.62, 0.22) * mm});
            skLineSegment(sketch, "E395", {"start": v(0.62, 0.22) * mm, "end": v(0.61, 0.22) * mm});
            skLineSegment(sketch, "E396", {"start": v(0.61, 0.22) * mm, "end": v(0.59, 0.23) * mm});
            skLineSegment(sketch, "E397", {"start": v(0.59, 0.23) * mm, "end": v(0.51, 0.24) * mm});
            skLineSegment(sketch, "E398", {"start": v(0.51, 0.24) * mm, "end": v(0.4, 0.24) * mm});
            skLineSegment(sketch, "E399", {"start": v(0.4, 0.24) * mm, "end": v(0.3, 0.2) * mm});
            skLineSegment(sketch, "E400", {"start": v(0.3, 0.2) * mm, "end": v(0.25, 0.14) * mm});
            skLineSegment(sketch, "E401", {"start": v(0.25, 0.14) * mm, "end": v(0.24, 0.11) * mm});
            skLineSegment(sketch, "E402", {"start": v(0.24, 0.11) * mm, "end": v(0.22, 0.09) * mm});
            skLineSegment(sketch, "E403", {"start": v(0.22, 0.09) * mm, "end": v(0.19, 0) * mm});
            skLineSegment(sketch, "E404", {"start": v(0.19, 0) * mm, "end": v(0.15, -0.13) * mm});
            skLineSegment(sketch, "E405", {"start": v(0.15, -0.13) * mm, "end": v(0.14, -0.23) * mm});
            skLineSegment(sketch, "E406", {"start": v(0.14, -0.23) * mm, "end": v(0.13, -0.29) * mm});
            skLineSegment(sketch, "E407", {"start": v(0.13, -0.29) * mm, "end": v(0.13, -0.3) * mm});
            skLineSegment(sketch, "E408", {"start": v(0.13, -0.3) * mm, "end": v(0.14, -0.3) * mm});
            skLineSegment(sketch, "E409", {"start": v(0.14, -0.3) * mm, "end": v(0.2, -0.32) * mm});
            skLineSegment(sketch, "E410", {"start": v(0.2, -0.32) * mm, "end": v(0.2, -0.32) * mm});
            skLineSegment(sketch, "E411", {"start": v(0.2, -0.32) * mm, "end": v(0.2, -0.31) * mm});
            skLineSegment(sketch, "E412", {"start": v(0.2, -0.31) * mm, "end": v(0.2, -0.31) * mm});
            skLineSegment(sketch, "E413", {"start": v(0.2, -0.31) * mm, "end": v(0.21, -0.29) * mm});
            skLineSegment(sketch, "E414", {"start": v(0.21, -0.29) * mm, "end": v(0.23, -0.2) * mm});
            skLineSegment(sketch, "E415", {"start": v(0.23, -0.2) * mm, "end": v(0.28, -0.12) * mm});
            skLineSegment(sketch, "E416", {"start": v(0.28, -0.12) * mm, "end": v(0.34, -0.06) * mm});
            skLineSegment(sketch, "E417", {"start": v(0.34, -0.06) * mm, "end": v(0.4, -0.03) * mm});
            skLineSegment(sketch, "E418", {"start": v(0.4, -0.03) * mm, "end": v(0.41, -0.03) * mm});
            skLineSegment(sketch, "E419", {"start": v(0.41, -0.03) * mm, "end": v(0.42, -0.02) * mm});
            skLineSegment(sketch, "E420", {"start": v(0.42, -0.02) * mm, "end": v(0.46, -0.02) * mm});
            skLineSegment(sketch, "E421", {"start": v(0.46, -0.02) * mm, "end": v(0.5, -0.02) * mm});
            skLineSegment(sketch, "E422", {"start": v(0.5, -0.02) * mm, "end": v(0.55, -0.04) * mm});
            skLineSegment(sketch, "E423", {"start": v(0.55, -0.04) * mm, "end": v(0.58, -0.06) * mm});
            skLineSegment(sketch, "E424", {"start": v(0.58, -0.06) * mm, "end": v(0.59, -0.07) * mm});
            skLineSegment(sketch, "E425", {"start": v(0.21, -0.55) * mm, "end": v(0.21, -0.55) * mm});
            skLineSegment(sketch, "E426", {"start": v(0.21, -0.55) * mm, "end": v(0.2, -0.54) * mm});
            skLineSegment(sketch, "E427", {"start": v(0.2, -0.54) * mm, "end": v(0.2, -0.53) * mm});
            skLineSegment(sketch, "E428", {"start": v(0.2, -0.53) * mm, "end": v(0.2, -0.52) * mm});
            skLineSegment(sketch, "E429", {"start": v(0.2, -0.52) * mm, "end": v(0.2, -0.53) * mm});
            skLineSegment(sketch, "E430", {"start": v(0.2, -0.53) * mm, "end": v(0.13, -0.54) * mm});
            skLineSegment(sketch, "E431", {"start": v(0.13, -0.54) * mm, "end": v(0.12, -0.54) * mm});
            skLineSegment(sketch, "E432", {"start": v(0.12, -0.54) * mm, "end": v(0.13, -0.57) * mm});
            skLineSegment(sketch, "E433", {"start": v(0.13, -0.57) * mm, "end": v(0.14, -0.65) * mm});
            skLineSegment(sketch, "E434", {"start": v(0.14, -0.65) * mm, "end": v(0.19, -0.74) * mm});
            skLineSegment(sketch, "E435", {"start": v(0.19, -0.74) * mm, "end": v(0.25, -0.81) * mm});
            skLineSegment(sketch, "E436", {"start": v(0.25, -0.81) * mm, "end": v(0.31, -0.86) * mm});
            skLineSegment(sketch, "E437", {"start": v(0.31, -0.86) * mm, "end": v(0.34, -0.87) * mm});
            skLineSegment(sketch, "E438", {"start": v(0.34, -0.87) * mm, "end": v(0.36, -0.86) * mm});
            skLineSegment(sketch, "E439", {"start": v(0.36, -0.86) * mm, "end": v(0.47, -0.8) * mm});
            skLineSegment(sketch, "E440", {"start": v(0.47, -0.8) * mm, "end": v(0.56, -0.75) * mm});
            skLineSegment(sketch, "E441", {"start": v(0.56, -0.75) * mm, "end": v(0.57, -0.74) * mm});
            skLineSegment(sketch, "E442", {"start": v(0.57, -0.74) * mm, "end": v(0.54, -0.75) * mm});
            skLineSegment(sketch, "E443", {"start": v(0.54, -0.75) * mm, "end": v(0.47, -0.75) * mm});
            skLineSegment(sketch, "E444", {"start": v(0.47, -0.75) * mm, "end": v(0.4, -0.73) * mm});
            skLineSegment(sketch, "E445", {"start": v(0.4, -0.73) * mm, "end": v(0.33, -0.7) * mm});
            skLineSegment(sketch, "E446", {"start": v(0.33, -0.7) * mm, "end": v(0.28, -0.67) * mm});
            skLineSegment(sketch, "E447", {"start": v(0.28, -0.67) * mm, "end": v(0.25, -0.63) * mm});
            skLineSegment(sketch, "E448", {"start": v(0.25, -0.63) * mm, "end": v(0.23, -0.6) * mm});
            skLineSegment(sketch, "E449", {"start": v(0.23, -0.6) * mm, "end": v(0.22, -0.57) * mm});
            skLineSegment(sketch, "E450", {"start": v(0.22, -0.57) * mm, "end": v(0.21, -0.55) * mm});
            skLineSegment(sketch, "E451", {"start": v(0.46, 0.47) * mm, "end": v(0.48, 0.48) * mm});
            skLineSegment(sketch, "E452", {"start": v(0.48, 0.48) * mm, "end": v(0.57, 0.51) * mm});
            skLineSegment(sketch, "E453", {"start": v(0.57, 0.51) * mm, "end": v(0.67, 0.52) * mm});
            skLineSegment(sketch, "E454", {"start": v(0.67, 0.52) * mm, "end": v(0.74, 0.5) * mm});
            skLineSegment(sketch, "E455", {"start": v(0.74, 0.5) * mm, "end": v(0.79, 0.49) * mm});
            skLineSegment(sketch, "E456", {"start": v(0.79, 0.49) * mm, "end": v(0.8, 0.48) * mm});
            skLineSegment(sketch, "E457", {"start": v(0.8, 0.48) * mm, "end": v(0.78, 0.52) * mm});
            skLineSegment(sketch, "E458", {"start": v(0.78, 0.52) * mm, "end": v(0.7, 0.62) * mm});
            skLineSegment(sketch, "E459", {"start": v(0.7, 0.62) * mm, "end": v(0.58, 0.73) * mm});
            skLineSegment(sketch, "E460", {"start": v(0.58, 0.73) * mm, "end": v(0.48, 0.8) * mm});
            skLineSegment(sketch, "E461", {"start": v(0.48, 0.8) * mm, "end": v(0.42, 0.84) * mm});
            skLineSegment(sketch, "E462", {"start": v(0.42, 0.84) * mm, "end": v(0.4, 0.85) * mm});
            skLineSegment(sketch, "E463", {"start": v(0.4, 0.85) * mm, "end": v(0.4, 0.84) * mm});
            skLineSegment(sketch, "E464", {"start": v(0.4, 0.84) * mm, "end": v(0.43, 0.8) * mm});
            skLineSegment(sketch, "E465", {"start": v(0.43, 0.8) * mm, "end": v(0.46, 0.75) * mm});
            skLineSegment(sketch, "E466", {"start": v(0.46, 0.75) * mm, "end": v(0.48, 0.69) * mm});
            skLineSegment(sketch, "E467", {"start": v(0.48, 0.69) * mm, "end": v(0.5, 0.63) * mm});
            skLineSegment(sketch, "E468", {"start": v(0.5, 0.63) * mm, "end": v(0.5, 0.61) * mm});
            skLineSegment(sketch, "E469", {"start": v(0.5, 0.61) * mm, "end": v(0.5, 0.6) * mm});
            skLineSegment(sketch, "E470", {"start": v(0.5, 0.6) * mm, "end": v(0.49, 0.54) * mm});
            skLineSegment(sketch, "E471", {"start": v(0.49, 0.54) * mm, "end": v(0.46, 0.48) * mm});
            skLineSegment(sketch, "E472", {"start": v(0.46, 0.48) * mm, "end": v(0.46, 0.47) * mm});
            skLineSegment(sketch, "E473", {"start": v(0, -0.55) * mm, "end": v(0, -0.55) * mm});
            skLineSegment(sketch, "E474", {"start": v(0, -0.55) * mm, "end": v(-0.02, -0.55) * mm});
            skLineSegment(sketch, "E475", {"start": v(-0.02, -0.55) * mm, "end": v(-0.04, -0.55) * mm});
            skLineSegment(sketch, "E476", {"start": v(-0.04, -0.55) * mm, "end": v(-0.04, -0.55) * mm});
            skLineSegment(sketch, "E477", {"start": v(-0.04, -0.55) * mm, "end": v(-0.04, -0.57) * mm});
            skLineSegment(sketch, "E478", {"start": v(-0.04, -0.57) * mm, "end": v(-0.05, -0.64) * mm});
            skLineSegment(sketch, "E479", {"start": v(-0.05, -0.64) * mm, "end": v(-0.07, -0.74) * mm});
            skLineSegment(sketch, "E480", {"start": v(-0.07, -0.74) * mm, "end": v(-0.11, -0.83) * mm});
            skLineSegment(sketch, "E481", {"start": v(-0.11, -0.83) * mm, "end": v(-0.16, -0.9) * mm});
            skLineSegment(sketch, "E482", {"start": v(-0.16, -0.9) * mm, "end": v(-0.18, -0.91) * mm});
            skLineSegment(sketch, "E483", {"start": v(-0.18, -0.91) * mm, "end": v(-0.17, -0.92) * mm});
            skLineSegment(sketch, "E484", {"start": v(-0.17, -0.92) * mm, "end": v(-0.13, -0.92) * mm});
            skLineSegment(sketch, "E485", {"start": v(-0.13, -0.92) * mm, "end": v(-0.07, -0.93) * mm});
            skLineSegment(sketch, "E486", {"start": v(-0.07, -0.93) * mm, "end": v(-0.03, -0.93) * mm});
            skLineSegment(sketch, "E487", {"start": v(-0.03, -0.93) * mm, "end": v(0, -0.93) * mm});
            skLineSegment(sketch, "E488", {"start": v(0, -0.93) * mm, "end": v(0, -0.93) * mm});
            skLineSegment(sketch, "E489", {"start": v(0, -0.93) * mm, "end": v(0.03, -0.93) * mm});
            skLineSegment(sketch, "E490", {"start": v(0.03, -0.93) * mm, "end": v(0.07, -0.93) * mm});
            skLineSegment(sketch, "E491", {"start": v(0.07, -0.93) * mm, "end": v(0.13, -0.92) * mm});
            skLineSegment(sketch, "E492", {"start": v(0.13, -0.92) * mm, "end": v(0.17, -0.92) * mm});
            skLineSegment(sketch, "E493", {"start": v(0.17, -0.92) * mm, "end": v(0.18, -0.91) * mm});
            skLineSegment(sketch, "E494", {"start": v(0.18, -0.91) * mm, "end": v(0.16, -0.9) * mm});
            skLineSegment(sketch, "E495", {"start": v(0.16, -0.9) * mm, "end": v(0.11, -0.83) * mm});
            skLineSegment(sketch, "E496", {"start": v(0.11, -0.83) * mm, "end": v(0.07, -0.74) * mm});
            skLineSegment(sketch, "E497", {"start": v(0.07, -0.74) * mm, "end": v(0.05, -0.64) * mm});
            skLineSegment(sketch, "E498", {"start": v(0.05, -0.64) * mm, "end": v(0.04, -0.57) * mm});
            skLineSegment(sketch, "E499", {"start": v(0.04, -0.57) * mm, "end": v(0.04, -0.55) * mm});
            skLineSegment(sketch, "E500", {"start": v(0.04, -0.55) * mm, "end": v(0.04, -0.55) * mm});
            skLineSegment(sketch, "E501", {"start": v(0.04, -0.55) * mm, "end": v(0.02, -0.55) * mm});
            skLineSegment(sketch, "E502", {"start": v(0.02, -0.55) * mm, "end": v(0, -0.55) * mm});
            skLineSegment(sketch, "E503", {"start": v(0.76, -0.41) * mm, "end": v(0.75, -0.42) * mm});
            skLineSegment(sketch, "E504", {"start": v(0.75, -0.42) * mm, "end": v(0.73, -0.42) * mm});
            skLineSegment(sketch, "E505", {"start": v(0.73, -0.42) * mm, "end": v(0.68, -0.43) * mm});
            skLineSegment(sketch, "E506", {"start": v(0.68, -0.43) * mm, "end": v(0.63, -0.44) * mm});
            skLineSegment(sketch, "E507", {"start": v(0.63, -0.44) * mm, "end": v(0.57, -0.44) * mm});
            skLineSegment(sketch, "E508", {"start": v(0.57, -0.44) * mm, "end": v(0.5, -0.42) * mm});
            skLineSegment(sketch, "E509", {"start": v(0.5, -0.42) * mm, "end": v(0.44, -0.39) * mm});
            skLineSegment(sketch, "E510", {"start": v(0.44, -0.39) * mm, "end": v(0.37, -0.33) * mm});
            skLineSegment(sketch, "E511", {"start": v(0.37, -0.33) * mm, "end": v(0.31, -0.27) * mm});
            skLineSegment(sketch, "E512", {"start": v(0.31, -0.27) * mm, "end": v(0.3, -0.25) * mm});
            skLineSegment(sketch, "E513", {"start": v(0.3, -0.25) * mm, "end": v(0.3, -0.26) * mm});
            skLineSegment(sketch, "E514", {"start": v(0.3, -0.26) * mm, "end": v(0.29, -0.3) * mm});
            skLineSegment(sketch, "E515", {"start": v(0.29, -0.3) * mm, "end": v(0.28, -0.35) * mm});
            skLineSegment(sketch, "E516", {"start": v(0.28, -0.35) * mm, "end": v(0.28, -0.36) * mm});
            skLineSegment(sketch, "E517", {"start": v(0.28, -0.36) * mm, "end": v(0.3, -0.36) * mm});
            skLineSegment(sketch, "E518", {"start": v(0.3, -0.36) * mm, "end": v(0.31, -0.4) * mm});
            skLineSegment(sketch, "E519", {"start": v(0.31, -0.4) * mm, "end": v(0.32, -0.41) * mm});
            skLineSegment(sketch, "E520", {"start": v(0.32, -0.41) * mm, "end": v(0.32, -0.42) * mm});
            skLineSegment(sketch, "E521", {"start": v(0.32, -0.42) * mm, "end": v(0.32, -0.43) * mm});
            skLineSegment(sketch, "E522", {"start": v(0.32, -0.43) * mm, "end": v(0.31, -0.45) * mm});
            skLineSegment(sketch, "E523", {"start": v(0.31, -0.45) * mm, "end": v(0.3, -0.48) * mm});
            skLineSegment(sketch, "E524", {"start": v(0.3, -0.48) * mm, "end": v(0.29, -0.48) * mm});
            skLineSegment(sketch, "E525", {"start": v(0.29, -0.48) * mm, "end": v(0.3, -0.5) * mm});
            skLineSegment(sketch, "E526", {"start": v(0.3, -0.5) * mm, "end": v(0.31, -0.54) * mm});
            skLineSegment(sketch, "E527", {"start": v(0.31, -0.54) * mm, "end": v(0.35, -0.59) * mm});
            skLineSegment(sketch, "E528", {"start": v(0.35, -0.59) * mm, "end": v(0.4, -0.62) * mm});
            skLineSegment(sketch, "E529", {"start": v(0.4, -0.62) * mm, "end": v(0.44, -0.64) * mm});
            skLineSegment(sketch, "E530", {"start": v(0.44, -0.64) * mm, "end": v(0.46, -0.64) * mm});
            skLineSegment(sketch, "E531", {"start": v(0.46, -0.64) * mm, "end": v(0.48, -0.65) * mm});
            skLineSegment(sketch, "E532", {"start": v(0.48, -0.65) * mm, "end": v(0.55, -0.64) * mm});
            skLineSegment(sketch, "E533", {"start": v(0.55, -0.64) * mm, "end": v(0.62, -0.63) * mm});
            skLineSegment(sketch, "E534", {"start": v(0.62, -0.63) * mm, "end": v(0.69, -0.6) * mm});
            skLineSegment(sketch, "E535", {"start": v(0.69, -0.6) * mm, "end": v(0.74, -0.55) * mm});
            skLineSegment(sketch, "E536", {"start": v(0.74, -0.55) * mm, "end": v(0.79, -0.5) * mm});
            skLineSegment(sketch, "E537", {"start": v(0.79, -0.5) * mm, "end": v(0.82, -0.44) * mm});
            skLineSegment(sketch, "E538", {"start": v(0.82, -0.44) * mm, "end": v(0.85, -0.38) * mm});
            skLineSegment(sketch, "E539", {"start": v(0.85, -0.38) * mm, "end": v(0.87, -0.34) * mm});
            skLineSegment(sketch, "E540", {"start": v(0.87, -0.34) * mm, "end": v(0.87, -0.33) * mm});
            skLineSegment(sketch, "E541", {"start": v(0.87, -0.33) * mm, "end": v(0.87, -0.34) * mm});
            skLineSegment(sketch, "E542", {"start": v(0.87, -0.34) * mm, "end": v(0.83, -0.37) * mm});
            skLineSegment(sketch, "E543", {"start": v(0.83, -0.37) * mm, "end": v(0.77, -0.4) * mm});
            skLineSegment(sketch, "E544", {"start": v(0.77, -0.4) * mm, "end": v(0.76, -0.41) * mm});
            skLineSegment(sketch, "E545", {"start": v(-0.3, 0.36) * mm, "end": v(-0.3, 0.37) * mm});
            skLineSegment(sketch, "E546", {"start": v(-0.3, 0.37) * mm, "end": v(-0.31, 0.42) * mm});
            skLineSegment(sketch, "E547", {"start": v(-0.31, 0.42) * mm, "end": v(-0.32, 0.47) * mm});
            skLineSegment(sketch, "E548", {"start": v(-0.32, 0.47) * mm, "end": v(-0.32, 0.48) * mm});
            skLineSegment(sketch, "E549", {"start": v(-0.32, 0.48) * mm, "end": v(-0.32, 0.52) * mm});
            skLineSegment(sketch, "E550", {"start": v(-0.32, 0.52) * mm, "end": v(-0.3, 0.64) * mm});
            skLineSegment(sketch, "E551", {"start": v(-0.3, 0.64) * mm, "end": v(-0.23, 0.76) * mm});
            skLineSegment(sketch, "E552", {"start": v(-0.23, 0.76) * mm, "end": v(-0.15, 0.86) * mm});
            skLineSegment(sketch, "E553", {"start": v(-0.15, 0.86) * mm, "end": v(-0.1, 0.92) * mm});
            skLineSegment(sketch, "E554", {"start": v(-0.1, 0.92) * mm, "end": v(-0.08, 0.93) * mm});
            skLineSegment(sketch, "E555", {"start": v(-0.08, 0.93) * mm, "end": v(-0.1, 0.93) * mm});
            skLineSegment(sketch, "E556", {"start": v(-0.1, 0.93) * mm, "end": v(-0.17, 0.9) * mm});
            skLineSegment(sketch, "E557", {"start": v(-0.17, 0.9) * mm, "end": v(-0.25, 0.85) * mm});
            skLineSegment(sketch, "E558", {"start": v(-0.25, 0.85) * mm, "end": v(-0.31, 0.8) * mm});
            skLineSegment(sketch, "E559", {"start": v(-0.31, 0.8) * mm, "end": v(-0.35, 0.74) * mm});
            skLineSegment(sketch, "E560", {"start": v(-0.35, 0.74) * mm, "end": v(-0.36, 0.72) * mm});
            skLineSegment(sketch, "E561", {"start": v(-0.36, 0.72) * mm, "end": v(-0.36, 0.71) * mm});
            skLineSegment(sketch, "E562", {"start": v(-0.36, 0.71) * mm, "end": v(-0.38, 0.66) * mm});
            skLineSegment(sketch, "E563", {"start": v(-0.38, 0.66) * mm, "end": v(-0.39, 0.6) * mm});
            skLineSegment(sketch, "E564", {"start": v(-0.39, 0.6) * mm, "end": v(-0.39, 0.6) * mm});
            skLineSegment(sketch, "E565", {"start": v(-0.39, 0.6) * mm, "end": v(-0.39, 0.56) * mm});
            skLineSegment(sketch, "E566", {"start": v(-0.39, 0.56) * mm, "end": v(-0.36, 0.47) * mm});
            skLineSegment(sketch, "E567", {"start": v(-0.36, 0.47) * mm, "end": v(-0.31, 0.37) * mm});
            skLineSegment(sketch, "E568", {"start": v(-0.31, 0.37) * mm, "end": v(-0.3, 0.36) * mm});
            skLineSegment(sketch, "E569", {"start": v(0.3, 0.36) * mm, "end": v(0.3, 0.37) * mm});
            skLineSegment(sketch, "E570", {"start": v(0.3, 0.37) * mm, "end": v(0.3, 0.42) * mm});
            skLineSegment(sketch, "E571", {"start": v(0.3, 0.42) * mm, "end": v(0.31, 0.47) * mm});
            skLineSegment(sketch, "E572", {"start": v(0.31, 0.47) * mm, "end": v(0.31, 0.48) * mm});
            skLineSegment(sketch, "E573", {"start": v(0.31, 0.48) * mm, "end": v(0.31, 0.52) * mm});
            skLineSegment(sketch, "E574", {"start": v(0.31, 0.52) * mm, "end": v(0.29, 0.64) * mm});
            skLineSegment(sketch, "E575", {"start": v(0.29, 0.64) * mm, "end": v(0.23, 0.76) * mm});
            skLineSegment(sketch, "E576", {"start": v(0.23, 0.76) * mm, "end": v(0.15, 0.86) * mm});
            skLineSegment(sketch, "E577", {"start": v(0.15, 0.86) * mm, "end": v(0.1, 0.92) * mm});
            skLineSegment(sketch, "E578", {"start": v(0.1, 0.92) * mm, "end": v(0.08, 0.93) * mm});
            skLineSegment(sketch, "E579", {"start": v(0.08, 0.93) * mm, "end": v(0.1, 0.93) * mm});
            skLineSegment(sketch, "E580", {"start": v(0.1, 0.93) * mm, "end": v(0.17, 0.9) * mm});
            skLineSegment(sketch, "E581", {"start": v(0.17, 0.9) * mm, "end": v(0.25, 0.85) * mm});
            skLineSegment(sketch, "E582", {"start": v(0.25, 0.85) * mm, "end": v(0.31, 0.8) * mm});
            skLineSegment(sketch, "E583", {"start": v(0.31, 0.8) * mm, "end": v(0.35, 0.74) * mm});
            skLineSegment(sketch, "E584", {"start": v(0.35, 0.74) * mm, "end": v(0.36, 0.72) * mm});
            skLineSegment(sketch, "E585", {"start": v(0.36, 0.72) * mm, "end": v(0.36, 0.71) * mm});
            skLineSegment(sketch, "E586", {"start": v(0.36, 0.71) * mm, "end": v(0.38, 0.66) * mm});
            skLineSegment(sketch, "E587", {"start": v(0.38, 0.66) * mm, "end": v(0.38, 0.6) * mm});
            skLineSegment(sketch, "E588", {"start": v(0.38, 0.6) * mm, "end": v(0.38, 0.6) * mm});
            skLineSegment(sketch, "E589", {"start": v(0.38, 0.6) * mm, "end": v(0.38, 0.56) * mm});
            skLineSegment(sketch, "E590", {"start": v(0.38, 0.56) * mm, "end": v(0.36, 0.47) * mm});
            skLineSegment(sketch, "E591", {"start": v(0.36, 0.47) * mm, "end": v(0.31, 0.37) * mm});
            skLineSegment(sketch, "E592", {"start": v(0.31, 0.37) * mm, "end": v(0.3, 0.36) * mm});
            skPoint(sketch, "E593.middle", {"position": v(0, 0) * mm});
            skCircle(sketch, "E594", {"center": v(0, 0) * mm, "radius": 1 * mm});
            skSolve(sketch);
        }
        {
            var Q0;
            Q0=makeQuery(id+"F0.imprint","IMPRINT",FACE,{"disambiguationData":[TD([[makeQuery(id+"F0.imprint","IMPRINT",EDGE,{"derivedFrom":sQuery(id+"F0.wireOp",EDGE,"E0")}),-1.0]])]});
            extrude(context, id + "F1", {"entities" : qUnion([Q0]), "depth" : 0.03 * mm, "offsetDistance" : 25 * mm});
        }
    });
